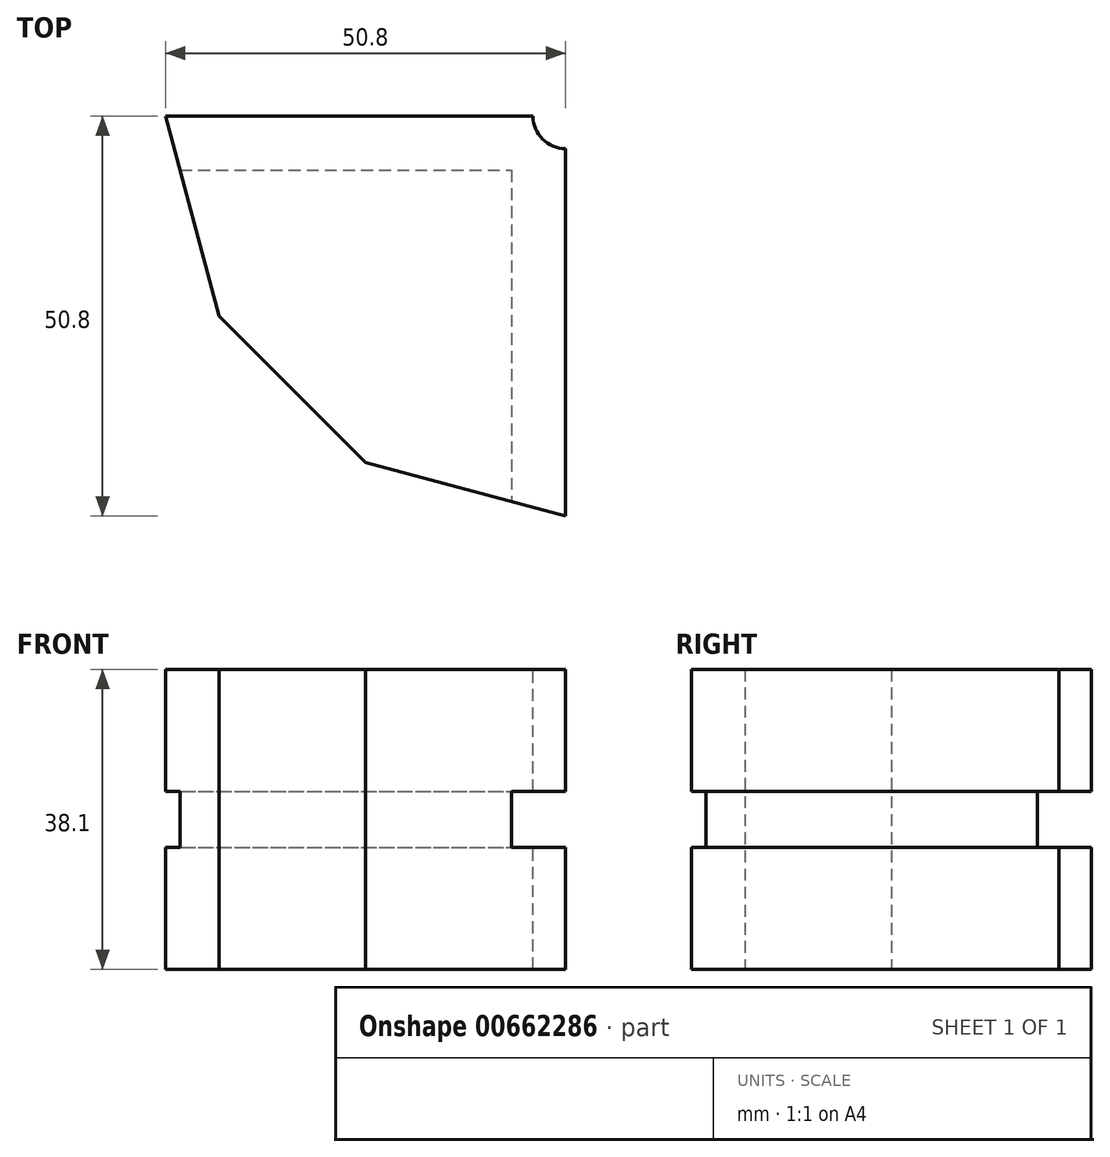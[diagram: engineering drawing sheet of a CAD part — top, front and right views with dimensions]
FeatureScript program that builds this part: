
annotation { "Feature Type Name" : "Feature", "Feature Type Description" : "" }
export const myFeature = defineFeature(function(context is Context, id is Id, definition is map)
    precondition{}
    {
        {
            var Q0;
            Q0=qCreatedBy(makeId("Top.planeOp"),FACE);
            var sketch = newSketch(context, id + "F0", { "sketchPlane" : qUnion([Q0])});
            skLineSegment(sketch, "E0.3", {"start": v(0, -50.8) * mm, "end": v(-25.4, -44) * mm});
            skLineSegment(sketch, "E0.4", {"start": v(-25.4, -44) * mm, "end": v(-44, -25.4) * mm});
            skLineSegment(sketch, "E0.5", {"start": v(-44, -25.4) * mm, "end": v(-50.8, 0) * mm});
            skLineSegment(sketch, "E1", {"start": v(-50.8, 0) * mm, "end": v(0, 0) * mm});
            skLineSegment(sketch, "E2", {"start": v(0, 0) * mm, "end": v(0, -50.8) * mm});
            skPoint(sketch, "E0.0.start.orphan", {"position": v(50.8, 0) * mm});
            skSolve(sketch);
        }
        {
            var Q0;
            Q0=qSketchRegion(id+"F0",true);
            extrude(context, id + "F1", {"entities" : qUnion([Q0]), "depth" : 38.1 * mm, "offsetDistance" : 25.4 * mm});
        }
        {
            var Q0;
            Q0=makeQuery(id+"F1.opExtrude","SWEPT_FACE",FACE,{"disambiguationData":[OSD([sQuery(id+"F0.wireOp",EDGE,"E1")])]});
            var sketch = newSketch(context, id + "F2", { "sketchPlane" : qUnion([Q0])});
            skPoint(sketch, "E3", {"position": v(25.4, 19.05) * mm});
            skLineSegment(sketch, "E4.bottom", {"start": v(50.8, 15.5) * mm, "end": v(0, 15.5) * mm});
            skLineSegment(sketch, "E4.top", {"start": v(50.8, 22.6) * mm, "end": v(0, 22.6) * mm});
            skLineSegment(sketch, "E4.left", {"start": v(50.8, 15.5) * mm, "end": v(50.8, 22.6) * mm});
            skLineSegment(sketch, "E4.right", {"start": v(0, 15.5) * mm, "end": v(0, 22.6) * mm});
            skPoint(sketch, "E5.orphan", {"position": v(0, 19.05) * mm});
            skPoint(sketch, "E6.end.orphan", {"position": v(50.8, 19.05) * mm});
            skSolve(sketch);
        }
        {
            var Q0;
            Q0=makeQuery(id+"F1.opExtrude","SWEPT_FACE",FACE,{"disambiguationData":[OSD([sQuery(id+"F0.wireOp",EDGE,"E2")])]});
            var sketch = newSketch(context, id + "F3", { "sketchPlane" : qUnion([Q0])});
            skPoint(sketch, "E7.0", {"position": v(0, 22.6) * mm});
            skPoint(sketch, "E7.1", {"position": v(0, 15.5) * mm});
            skLineSegment(sketch, "E8", {"start": v(0, 22.6) * mm, "end": v(-50.8, 22.6) * mm});
            skLineSegment(sketch, "E9", {"start": v(0, 15.5) * mm, "end": v(-50.8, 15.5) * mm});
            skSolve(sketch);
        }
        {
            var Q0;
            {var subQ0=sQuery(id+"F3.wireOp",EDGE,"E8");Q0=makeQuery(id+"F3.imprint","IMPRINT",FACE,{"disambiguationData":[TD([[makeQuery(id+"F3.imprint","IMPRINT",EDGE,{"derivedFrom":subQ0}),1.0]])]});}
            extrude(context, id + "F4", {"entities" : qUnion([Q0]), "operationType" : NewBodyOperationType.REMOVE, "oppositeDirection" : true, "depth" : 6.86 * mm, "offsetDistance" : 25.4 * mm});
        }
        {
            var Q0;
            Q0=makeQuery(id+"F2.imprint","IMPRINT",FACE,{"disambiguationData":[TD([[makeQuery(id+"F2.imprint","IMPRINT",EDGE,{"derivedFrom":sQuery(id+"F2.wireOp",EDGE,"E4.bottom")}),-1.0]])]});
            extrude(context, id + "F5", {"entities" : qUnion([Q0]), "operationType" : NewBodyOperationType.REMOVE, "oppositeDirection" : true, "depth" : 6.86 * mm, "offsetDistance" : 25.4 * mm});
        }
        {
            var Q0;
            Q0=makeQuery(id+"F1.opExtrude","CAP_FACE",FACE,{"disambiguationData":[OSD([sQuery(id+"F0.wireOp",EDGE,"E0.3"),sQuery(id+"F0.wireOp",EDGE,"E0.4"),sQuery(id+"F0.wireOp",EDGE,"E0.5"),sQuery(id+"F0.wireOp",EDGE,"E1"),sQuery(id+"F0.wireOp",EDGE,"E2")])],"isStart":false});
            var sketch = newSketch(context, id + "F6", { "sketchPlane" : qUnion([Q0])});
            skCircle(sketch, "E10", {"center": v(0, 0) * mm, "radius": 4.13 * mm});
            skSolve(sketch);
        }
        {
            var Q0;
            Q0 = qSketchRegion(id + "F6", true);
            extrude(context, id + "F7", {"entities" : qUnion([Q0]), "operationType" : NewBodyOperationType.REMOVE, "oppositeDirection" : true, "depth" : 39.62 * mm, "offsetDistance" : 25.4 * mm});
        }
    });
